# Revit family: AP-15T
name_source: partatom
category: Communication Devices
revit_build: Autodesk Revit 2014 (Build: 20140709_2115(x64)
units: mm (PartAtom-declared; Revit-internal decimal feet)

## types (1)
- Horn Loudspeaker
    100V Taps = 2, 4, 8 and 15 watts
    25V Taps = .48, .94, 1.8, 7.5, and 15 watts
    70V Taps = 1, 2, 3.8, 7.5, and 15 watts
    Baffle Material = <By Category>
    Body Material = Default
    Color = <By Category>
    Cost = 128.99 $
    Cost MSRP = 128.99 $
    Coverage Horizontal = 0.00°
    Coverage Vertical = 27.00°
    Depth = 9.29 "
    Description = HORN LOUDSPEAKER WITH 15-WATT 25V/70V/100V TRANSFORMER
    Dispersion Angle = 70.00°
    Enclosure Material = <By Category>
    Family Code (default) = LOUD SPEAKERS
    Frequency Response  = 400 - 14,000 Hz (Nominal) 500 Hz - 6000 Hz (±5dB)
    Grill Material = <By Category>
    Height = 8.79 "
    IQ Category = SPEAKERS
    Impedance = 8
    Ingress Protection = IP-34
    Input Connectors = Barrier Terminal
    Manufacturer = ATLAS SOUND
    Manufacturer URL = https://www.atlasied.com
    Market = Commercial, Higher Education, Emergency
    MasterFormat = 27 41 13
    MaterFormat Title = SPEAKERS
    Model = AP-15T
    Mount Material = Default
    OmniClass Number = 23-37 17 13 19
    OmniClass Title = SPEAKERS
    Pitch = 0.00°
    Power Peak = 120
    Power Rating (RMS) = 15 Watts Continuous
    Product Documentation Link = https://www.atlasied.com
    Product Page URL = https://www.atlasied.com
    Rotation = 0.00°
    SPL Max = 107
    ScheduleType |RF| = AtlasIED Master
    Sensitivity = 106
    Speaker Dispersion = 70.00°
    Transformer Option = Yes
    URL = www.atlassound.com
    Vertical Symmetry = Yes
    Warranty = 5 Year
    Weight Product = 5
    Width = 8 "

## geometry (parser evidence)
native form markers: Blend x6, Sweep x2
no freeform markers — native parametric forms only
